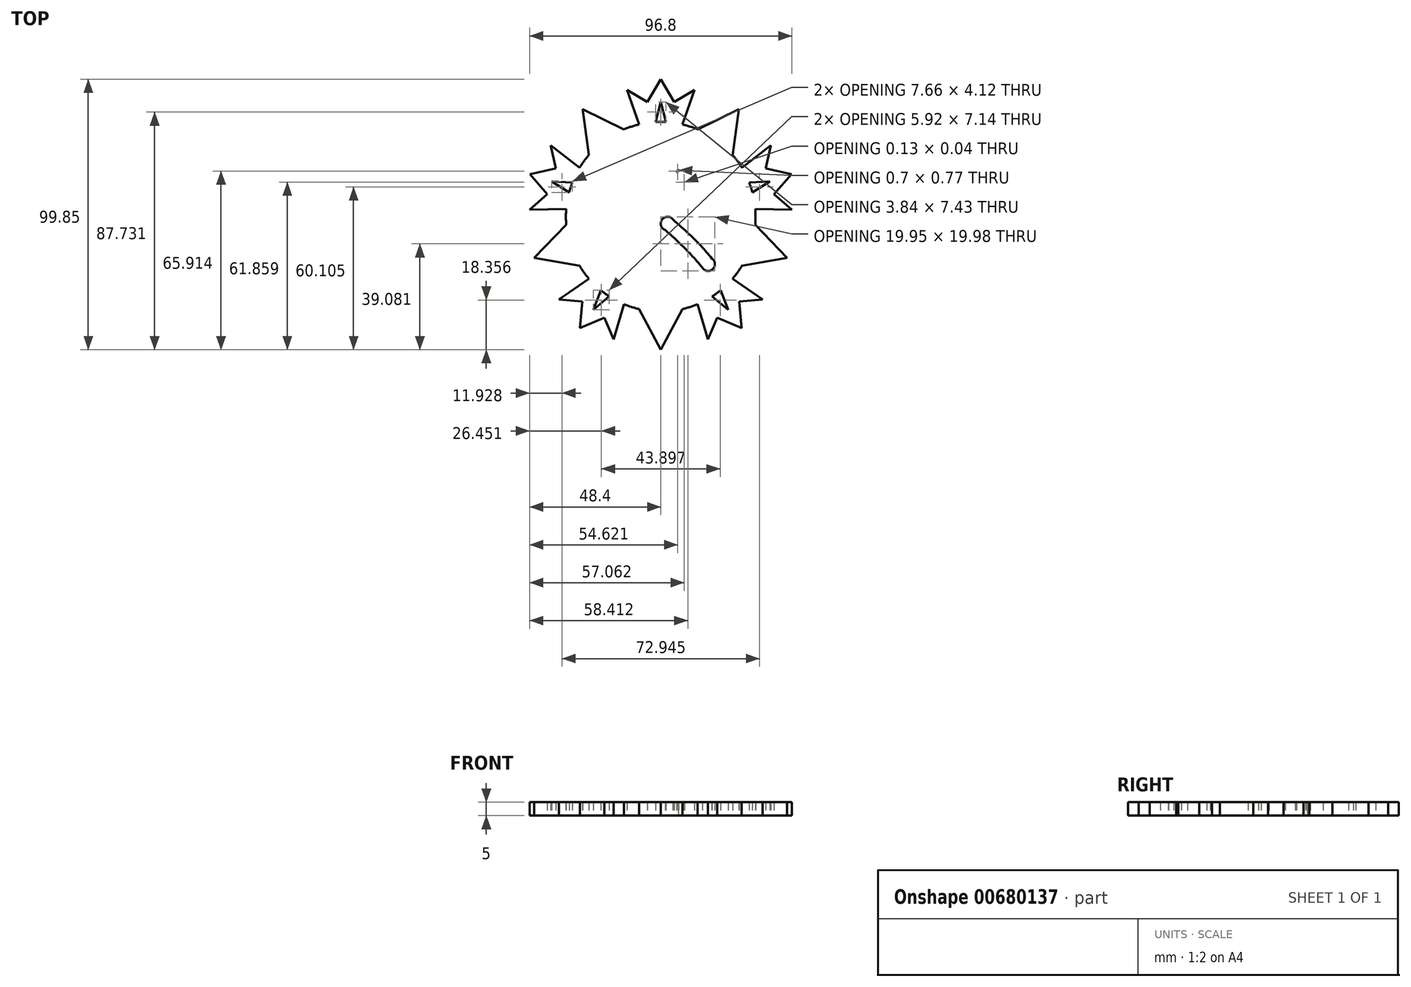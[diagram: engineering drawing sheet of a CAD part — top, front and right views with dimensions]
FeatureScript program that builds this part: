
annotation { "Feature Type Name" : "Feature", "Feature Type Description" : "" }
export const myFeature = defineFeature(function(context is Context, id is Id, definition is map)
    precondition{}
    {
        {
            var Q0;
            Q0=qCreatedBy(makeId("Top.planeOp"),FACE);
            var sketch = newSketch(context, id + "F0", { "sketchPlane" : qUnion([Q0])});
            skCircle(sketch, "E0", {"center": v(0, 0) * mm, "radius": 35 * mm});
            skArc(sketch, "E1", {"start": v(-14.63, 16.11) * mm, "mid": v(-17.95, 17.5) * mm, "end": v(-19.22, 14.13) * mm});
            skArc(sketch, "E2", {"start": v(-9.76, -5.79) * mm, "mid": v(-6.86, -7.22) * mm, "end": v(-4.97, -4.6) * mm});
            skLineSegment(sketch, "E3", {"start": v(-9.76, -5.79) * mm, "end": v(-19.22, 14.13) * mm});
            skLineSegment(sketch, "E4", {"start": v(-7.46, -2.3) * mm, "end": v(-14.63, 16.11) * mm});
            skArc(sketch, "E5", {"start": v(8.6, 12.77) * mm, "mid": v(10.05, 16.7) * mm, "end": v(5.87, 16.46) * mm});
            skFitSpline(sketch, "E6", {"points": [v(-4.97, -4.6) * mm, v(0, 4.75) * mm, v(8.73, 12.8) * mm, v(8.69, 12.6) * mm], "startDerivative": vector(6.67, 19.19) * mm, "endDerivative": vector(-2.05, -4.39) * mm});
            skFitSpline(sketch, "E7", {"points": [v(-7.46, -2.3) * mm, v(-2.2, 7.53) * mm, v(6.57, 17.23) * mm, v(5.87, 16.46) * mm], "startDerivative": vector(8.24, 21.14) * mm, "endDerivative": vector(-8.55, -9.52) * mm});
            skArc(sketch, "E8", {"start": v(4.48, -0.97) * mm, "mid": v(0.49, -1.01) * mm, "end": v(1.62, -4.84) * mm});
            skArc(sketch, "E9", {"start": v(15.34, -18.77) * mm, "mid": v(19.24, -19.3) * mm, "end": v(18.83, -15.38) * mm});
            skFitSpline(sketch, "E10", {"points": [v(4.48, -0.97) * mm, v(13.62, -9.42) * mm, v(18.83, -15.38) * mm], "startDerivative": vector(17.74, -15.67) * mm, "endDerivative": vector(10.7, -13.04) * mm});
            skFitSpline(sketch, "E11", {"points": [v(1.62, -4.84) * mm, v(9.57, -12.33) * mm, v(15.34, -18.77) * mm], "startDerivative": vector(15.78, -14.24) * mm, "endDerivative": vector(11.6, -13.57) * mm});
            skLineSegment(sketch, "E12", {"start": v(8, -34.07) * mm, "end": v(0, -49.07) * mm});
            skLineSegment(sketch, "E13", {"start": v(-8, -34.07) * mm, "end": v(0, -49.07) * mm});
            skLineSegment(sketch, "E14", {"start": v(-7.99, 34.08) * mm, "end": v(-12.5, 46.83) * mm});
            skLineSegment(sketch, "E15", {"start": v(-1.92, 34.95) * mm, "end": v(0, 42.37) * mm});
            skLineSegment(sketch, "E16", {"start": v(0, 42.37) * mm, "end": v(1.92, 34.95) * mm});
            skLineSegment(sketch, "E17", {"start": v(7.99, 34.08) * mm, "end": v(12.5, 46.83) * mm});
            skLineSegment(sketch, "E18", {"start": v(-12.5, 46.83) * mm, "end": v(-5, 42.37) * mm});
            skLineSegment(sketch, "E19", {"start": v(-5, 42.37) * mm, "end": v(0, 50.78) * mm});
            skLineSegment(sketch, "E20.MirrorCS", {"start": v(5, 42.37) * mm, "end": v(0, 50.78) * mm});
            skLineSegment(sketch, "E21.MirrorCS", {"start": v(12.5, 46.83) * mm, "end": v(5, 42.37) * mm});
            skLineSegment(sketch, "E22.MirrorCS", {"start": v(29.93, -18.14) * mm, "end": v(46.67, -15.16) * mm});
            skLineSegment(sketch, "E23.MirrorCS", {"start": v(34.88, -2.92) * mm, "end": v(46.67, -15.16) * mm});
            skLineSegment(sketch, "E24.MirrorCS", {"start": v(26.5, 22.86) * mm, "end": v(28.84, 39.7) * mm});
            skLineSegment(sketch, "E25.MirrorCS", {"start": v(13.56, 32.27) * mm, "end": v(28.84, 39.7) * mm});
            skLineSegment(sketch, "E26.MirrorCS", {"start": v(-34.88, -2.92) * mm, "end": v(-46.67, -15.16) * mm});
            skLineSegment(sketch, "E27.MirrorCS", {"start": v(-29.93, -18.14) * mm, "end": v(-46.67, -15.16) * mm});
            skLineSegment(sketch, "E28.MirrorCS", {"start": v(-13.56, 32.27) * mm, "end": v(-28.84, 39.7) * mm});
            skLineSegment(sketch, "E29.MirrorCS", {"start": v(-26.5, 22.86) * mm, "end": v(-28.84, 39.7) * mm});
            skLineSegment(sketch, "E30.MirrorCS", {"start": v(-34.88, 2.93) * mm, "end": v(-48.4, 2.58) * mm});
            skLineSegment(sketch, "E31.MirrorCS", {"start": v(-48.4, 2.58) * mm, "end": v(-41.85, 8.34) * mm});
            skLineSegment(sketch, "E32.MirrorCS", {"start": v(-41.85, 8.34) * mm, "end": v(-48.3, 15.7) * mm});
            skLineSegment(sketch, "E33.MirrorCS", {"start": v(-38.76, 17.85) * mm, "end": v(-48.3, 15.7) * mm});
            skLineSegment(sketch, "E34.MirrorCS", {"start": v(-29.94, 18.13) * mm, "end": v(-40.68, 26.36) * mm});
            skLineSegment(sketch, "E35.MirrorCS", {"start": v(-40.68, 26.36) * mm, "end": v(-38.76, 17.85) * mm});
            skLineSegment(sketch, "E36.MirrorCS", {"start": v(-32.64, 12.62) * mm, "end": v(-40.3, 13.1) * mm});
            skLineSegment(sketch, "E37.MirrorCS", {"start": v(-40.3, 13.1) * mm, "end": v(-33.83, 8.98) * mm});
            skLineSegment(sketch, "E38.MirrorCS", {"start": v(33.83, 8.98) * mm, "end": v(40.3, 13.1) * mm});
            skLineSegment(sketch, "E39.MirrorCS", {"start": v(40.3, 13.1) * mm, "end": v(32.64, 12.62) * mm});
            skLineSegment(sketch, "E40.MirrorCS", {"start": v(29.94, 18.13) * mm, "end": v(40.68, 26.36) * mm});
            skLineSegment(sketch, "E41.MirrorCS", {"start": v(40.68, 26.36) * mm, "end": v(38.76, 17.85) * mm});
            skLineSegment(sketch, "E42.MirrorCS", {"start": v(38.76, 17.85) * mm, "end": v(48.3, 15.7) * mm});
            skLineSegment(sketch, "E43.MirrorCS", {"start": v(41.85, 8.34) * mm, "end": v(48.3, 15.7) * mm});
            skLineSegment(sketch, "E44.MirrorCS", {"start": v(34.88, 2.93) * mm, "end": v(48.4, 2.58) * mm});
            skLineSegment(sketch, "E45.MirrorCS", {"start": v(48.4, 2.58) * mm, "end": v(41.85, 8.34) * mm});
            skLineSegment(sketch, "E46.MirrorCS", {"start": v(37.64, -30.54) * mm, "end": v(28.95, -31.34) * mm});
            skLineSegment(sketch, "E47.MirrorCS", {"start": v(28.95, -31.34) * mm, "end": v(29.85, -41.08) * mm});
            skLineSegment(sketch, "E48.MirrorCS", {"start": v(26.5, -22.87) * mm, "end": v(37.64, -30.54) * mm});
            skLineSegment(sketch, "E49.MirrorCS", {"start": v(22.1, -27.15) * mm, "end": v(24.9, -34.28) * mm});
            skLineSegment(sketch, "E50.MirrorCS", {"start": v(24.9, -34.28) * mm, "end": v(19, -29.4) * mm});
            skLineSegment(sketch, "E51.MirrorCS", {"start": v(20.86, -37.22) * mm, "end": v(29.85, -41.08) * mm});
            skLineSegment(sketch, "E52.MirrorCS", {"start": v(13.57, -32.26) * mm, "end": v(17.42, -45.24) * mm});
            skLineSegment(sketch, "E53.MirrorCS", {"start": v(17.42, -45.24) * mm, "end": v(20.86, -37.22) * mm});
            skLineSegment(sketch, "E54.MirrorCS", {"start": v(-24.9, -34.28) * mm, "end": v(-19, -29.4) * mm});
            skLineSegment(sketch, "E55.MirrorCS", {"start": v(-20.86, -37.22) * mm, "end": v(-29.85, -41.08) * mm});
            skLineSegment(sketch, "E56.MirrorCS", {"start": v(-17.42, -45.24) * mm, "end": v(-20.86, -37.22) * mm});
            skLineSegment(sketch, "E57.MirrorCS", {"start": v(-13.57, -32.26) * mm, "end": v(-17.42, -45.24) * mm});
            skLineSegment(sketch, "E58.MirrorCS", {"start": v(-22.1, -27.15) * mm, "end": v(-24.9, -34.28) * mm});
            skLineSegment(sketch, "E59.MirrorCS", {"start": v(-28.95, -31.34) * mm, "end": v(-29.85, -41.08) * mm});
            skLineSegment(sketch, "E60.MirrorCS", {"start": v(-26.5, -22.87) * mm, "end": v(-37.64, -30.54) * mm});
            skLineSegment(sketch, "E61.MirrorCS", {"start": v(-37.64, -30.54) * mm, "end": v(-28.95, -31.34) * mm});
            skSolve(sketch);
        }
        {
            var Q0;
            Q0=makeQuery(id+"F0.imprint","IMPRINT",FACE,{"disambiguationData":[TD([[makeQuery(id+"F0.imprint","IMPRINT",EDGE,{"derivedFrom":sQuery(id+"F0.wireOp",EDGE,"E1")}),-1.0]])]});
            var Q1;
            Q1=makeQuery(id+"F0.imprint","IMPRINT",FACE,{"disambiguationData":[TD([[makeQuery(id+"F0.imprint","IMPRINT",EDGE,{"derivedFrom":sQuery(id+"F0.wireOp",EDGE,"E46.MirrorCS")}),-1.0]])]});
            var Q2;
            {var subQ0=sQuery(id+"F0.wireOp",EDGE,"E24.MirrorCS");Q2=makeQuery(id+"F0.imprint","IMPRINT",FACE,{"disambiguationData":[TD([[makeQuery(id+"F0.imprint","IMPRINT",EDGE,{"derivedFrom":subQ0}),1.0]])]});}
            var Q3;
            {var subQ0=sQuery(id+"F0.wireOp",EDGE,"E28.MirrorCS");Q3=makeQuery(id+"F0.imprint","IMPRINT",FACE,{"disambiguationData":[TD([[makeQuery(id+"F0.imprint","IMPRINT",EDGE,{"derivedFrom":subQ0}),1.0]])]});}
            var Q4;
            {var subQ0=sQuery(id+"F0.wireOp",EDGE,"E26.MirrorCS");Q4=makeQuery(id+"F0.imprint","IMPRINT",FACE,{"disambiguationData":[TD([[makeQuery(id+"F0.imprint","IMPRINT",EDGE,{"derivedFrom":subQ0}),1.0]])]});}
            var Q5;
            {var subQ0=sQuery(id+"F0.wireOp",EDGE,"E12");Q5=makeQuery(id+"F0.imprint","IMPRINT",FACE,{"disambiguationData":[TD([[makeQuery(id+"F0.imprint","IMPRINT",EDGE,{"derivedFrom":subQ0}),-1.0]])]});}
            var Q6;
            {var subQ0=sQuery(id+"F0.wireOp",EDGE,"E22.MirrorCS");Q6=makeQuery(id+"F0.imprint","IMPRINT",FACE,{"disambiguationData":[TD([[makeQuery(id+"F0.imprint","IMPRINT",EDGE,{"derivedFrom":subQ0}),1.0]])]});}
            var Q7;
            {var subQ0=sQuery(id+"F0.wireOp",EDGE,"E38.MirrorCS");Q7=makeQuery(id+"F0.imprint","IMPRINT",FACE,{"disambiguationData":[TD([[makeQuery(id+"F0.imprint","IMPRINT",EDGE,{"derivedFrom":subQ0}),-1.0]])]});}
            var Q8;
            {var subQ0=sQuery(id+"F0.wireOp",EDGE,"E14");Q8=makeQuery(id+"F0.imprint","IMPRINT",FACE,{"disambiguationData":[TD([[makeQuery(id+"F0.imprint","IMPRINT",EDGE,{"derivedFrom":subQ0}),-1.0]])]});}
            var Q9;
            {var subQ0=sQuery(id+"F0.wireOp",EDGE,"E30.MirrorCS");Q9=makeQuery(id+"F0.imprint","IMPRINT",FACE,{"disambiguationData":[TD([[makeQuery(id+"F0.imprint","IMPRINT",EDGE,{"derivedFrom":subQ0}),-1.0]])]});}
            var Q10;
            {var subQ0=sQuery(id+"F0.wireOp",EDGE,"E54.MirrorCS");Q10=makeQuery(id+"F0.imprint","IMPRINT",FACE,{"disambiguationData":[TD([[makeQuery(id+"F0.imprint","IMPRINT",EDGE,{"derivedFrom":subQ0}),-1.0]])]});}
            var Q11;
            {var subQ0=sQuery(id+"F0.wireOp",EDGE,"E7");var subQ1=sQuery(id+"F0.wireOp",EDGE,"E5");var subQ2=makeQuery(id+"F0.imprint","INTERSECT",VERTEX,{"disambiguationData":[OD(0.0)],"derivedFrom":[subQ1,subQ0]});Q11=makeQuery(id+"F0.imprint","IMPRINT",FACE,{"disambiguationData":[TD([[makeQuery(id+"F0.imprint","IMPRINT",EDGE,{"disambiguationData":[TD([[subQ2,1.0]])],"derivedFrom":subQ1}),1.0]])]});}
            var Q12;
            {var subQ0=sQuery(id+"F0.wireOp",EDGE,"E6");var subQ1=sQuery(id+"F0.wireOp",EDGE,"E5");var subQ2=makeQuery(id+"F0.imprint","INTERSECT",VERTEX,{"disambiguationData":[OD(0.0)],"derivedFrom":[subQ1,subQ0]});Q12=makeQuery(id+"F0.imprint","IMPRINT",FACE,{"disambiguationData":[TD([[makeQuery(id+"F0.imprint","IMPRINT",EDGE,{"disambiguationData":[TD([[subQ2,-1.0]])],"derivedFrom":subQ1}),1.0]])]});}
            var Q13;
            {var subQ0=sQuery(id+"F0.wireOp",EDGE,"E7");var subQ1=sQuery(id+"F0.wireOp",EDGE,"E5");var subQ2=makeQuery(id+"F0.imprint","INTERSECT",VERTEX,{"disambiguationData":[OD(2.0)],"derivedFrom":[subQ1,subQ0]});Q13=makeQuery(id+"F0.imprint","IMPRINT",FACE,{"disambiguationData":[TD([[makeQuery(id+"F0.imprint","IMPRINT",EDGE,{"disambiguationData":[TD([[subQ2,-1.0]])],"derivedFrom":subQ1}),1.0]])]});}
            extrude(context, id + "F1", {"entities" : qUnion([Q0, Q1, Q2, Q3, Q4, Q5, Q6, Q7, Q8, Q9, Q10, Q11, Q12, Q13]), "depth" : 5 * mm, "offsetDistance" : 25 * mm});
        }
    });
